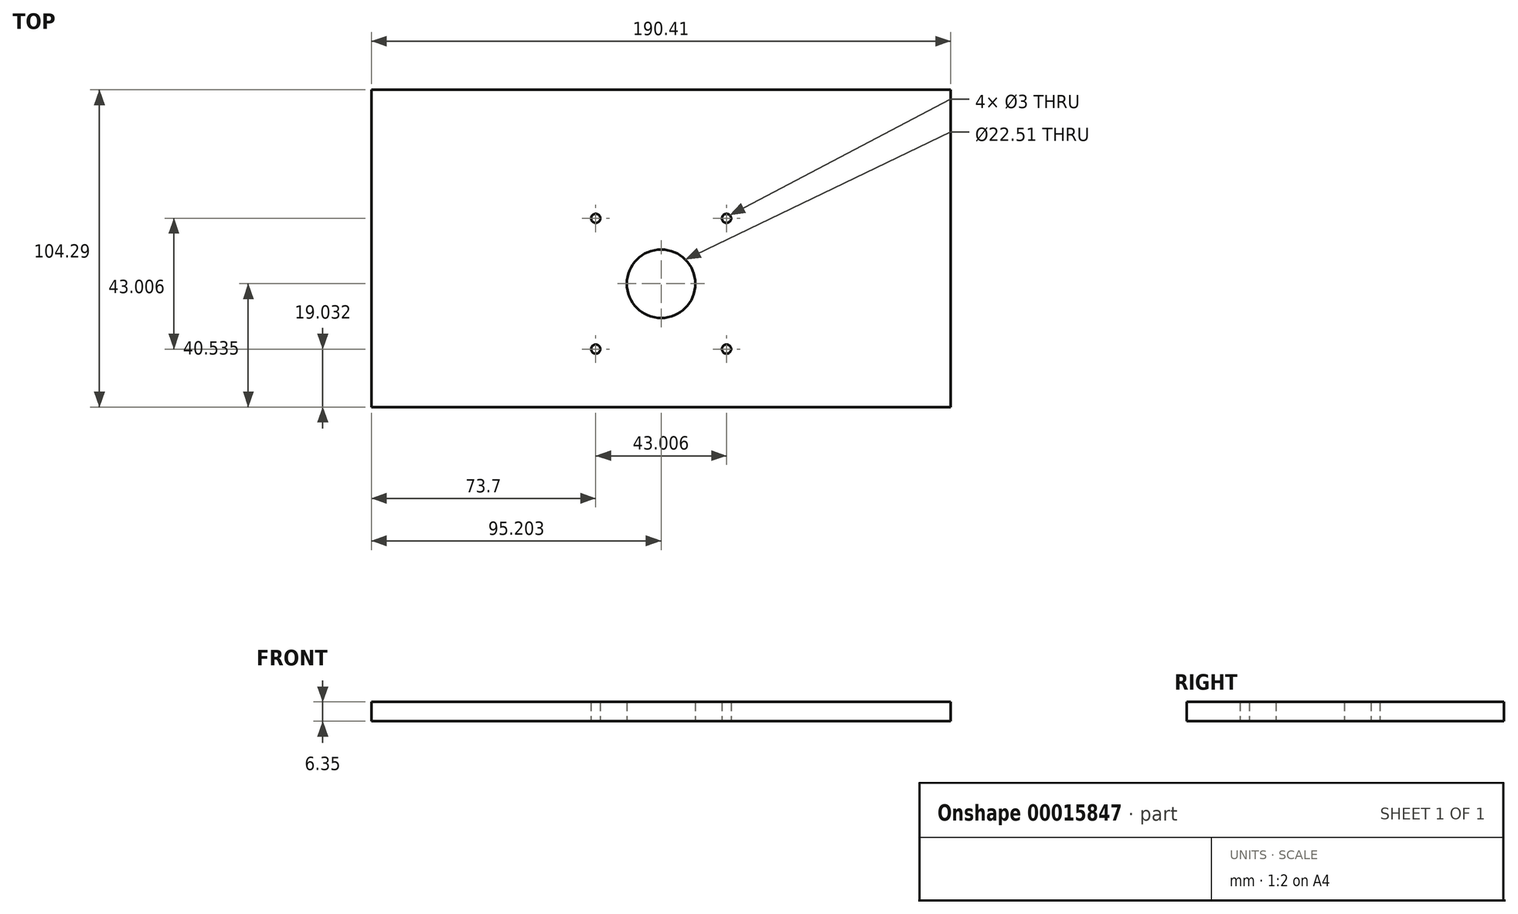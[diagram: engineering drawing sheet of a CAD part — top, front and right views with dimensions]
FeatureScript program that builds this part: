
annotation { "Feature Type Name" : "Feature", "Feature Type Description" : "" }
export const myFeature = defineFeature(function(context is Context, id is Id, definition is map)
    precondition{}
    {
        {
            var Q0;
            Q0=qCreatedBy(makeId("Top.planeOp"),FACE);
            var sketch = newSketch(context, id + "F0", { "sketchPlane" : qUnion([Q0])});
            skLineSegment(sketch, "E0.bottom", {"start": v(0, 0) * mm, "end": v(190.4, 0) * mm});
            skLineSegment(sketch, "E0.top", {"start": v(0, -104.3) * mm, "end": v(190.4, -104.3) * mm});
            skLineSegment(sketch, "E0.left", {"start": v(0, 0) * mm, "end": v(0, -104.3) * mm});
            skLineSegment(sketch, "E0.right", {"start": v(190.4, 0) * mm, "end": v(190.4, -104.3) * mm});
            skLineSegment(sketch, "E1.rect.bottom", {"start": v(116.7, -42.25) * mm, "end": v(73.7, -42.25) * mm, "construction": true});
            skLineSegment(sketch, "E1.rect.top", {"start": v(116.7, -85.26) * mm, "end": v(73.7, -85.26) * mm, "construction": true});
            skLineSegment(sketch, "E1.rect.left", {"start": v(116.7, -42.25) * mm, "end": v(116.7, -85.26) * mm, "construction": true});
            skLineSegment(sketch, "E1.rect.right", {"start": v(73.7, -42.25) * mm, "end": v(73.7, -85.26) * mm, "construction": true});
            skPoint(sketch, "E1.rect.middle", {"position": v(95.2, -63.75) * mm});
            skCircle(sketch, "E2", {"center": v(95.2, -63.75) * mm, "radius": 11.25 * mm});
            skCircle(sketch, "E3", {"center": v(116.7, -42.25) * mm, "radius": 1.5 * mm});
            skCircle(sketch, "E4", {"center": v(73.7, -42.25) * mm, "radius": 1.5 * mm});
            skCircle(sketch, "E5", {"center": v(73.7, -85.26) * mm, "radius": 1.5 * mm});
            skCircle(sketch, "E6", {"center": v(116.7, -85.26) * mm, "radius": 1.5 * mm});
            skLineSegment(sketch, "E7", {"start": v(95.2, -63.75) * mm, "end": v(95.2, 0) * mm});
            skSolve(sketch);
        }
        {
            var Q0;
            Q0=qSketchRegion(id+"F0",true);
            extrude(context, id + "F1", {"entities" : qUnion([Q0]), "depth" : 6.35 * mm});
        }
    });
